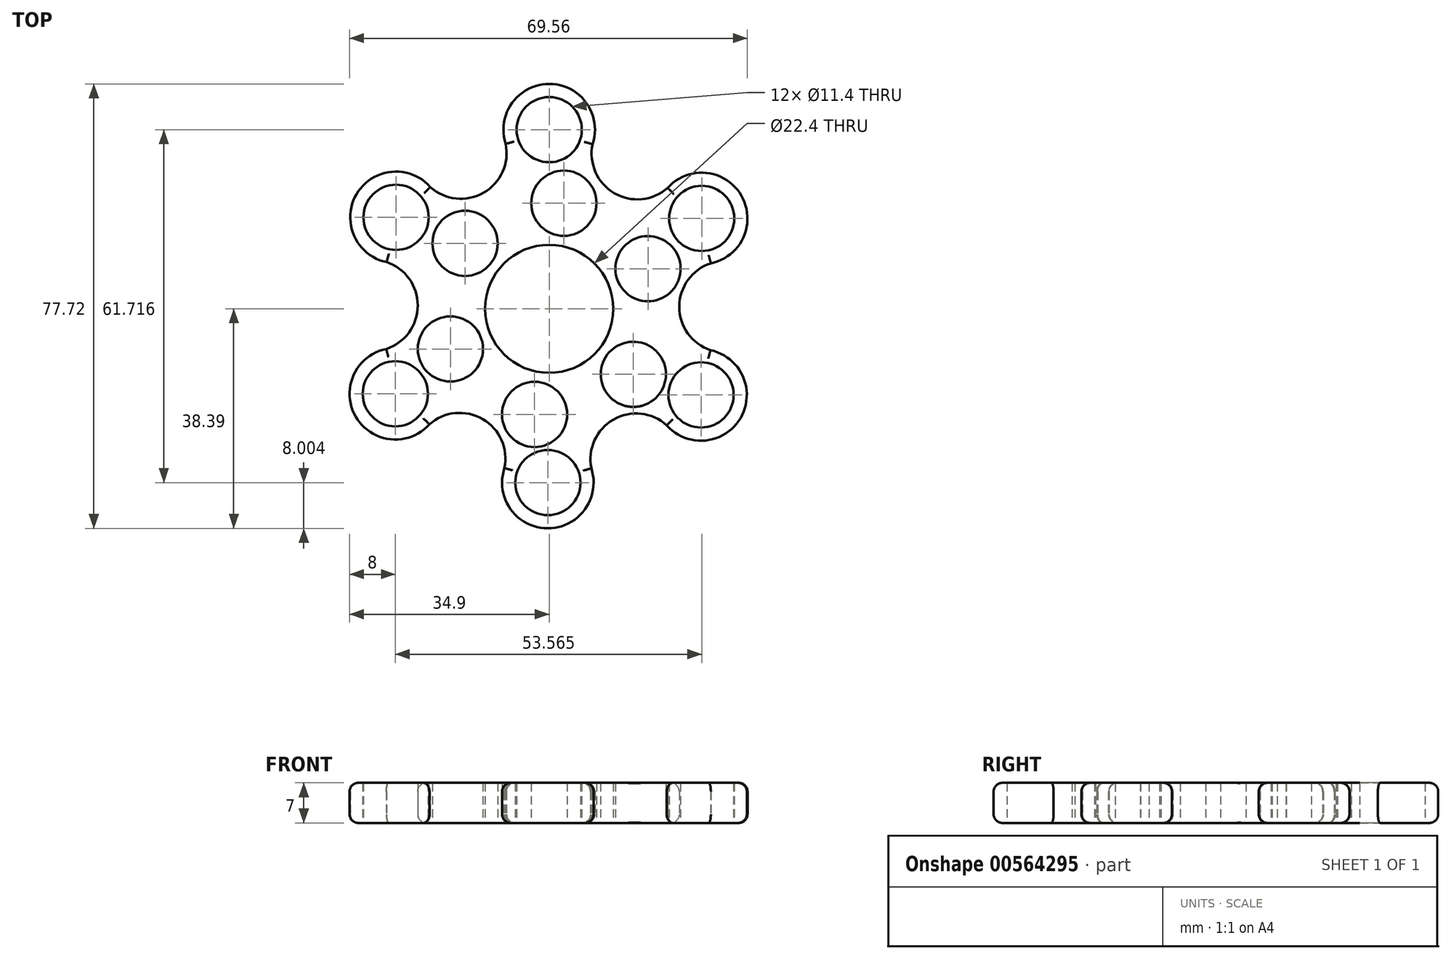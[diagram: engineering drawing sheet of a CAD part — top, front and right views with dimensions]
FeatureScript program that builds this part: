
annotation { "Feature Type Name" : "Feature", "Feature Type Description" : "" }
export const myFeature = defineFeature(function(context is Context, id is Id, definition is map)
    precondition{}
    {
        {
            var Q0;
            Q0=qCreatedBy(makeId("Top.planeOp"),FACE);
            var sketch = newSketch(context, id + "F0", { "sketchPlane" : qUnion([Q0])});
            skCircle(sketch, "E0", {"center": v(0, 0) * mm, "radius": 11.2 * mm});
            skArc(sketch, "E1", {"start": v(7.59, 28.79) * mm, "mid": v(0.03, 39.33) * mm, "end": v(-7.6, 28.85) * mm});
            skCircle(sketch, "E2", {"center": v(0, 31.33) * mm, "radius": 5.7 * mm});
            skArc(sketch, "E3.1.1", {"start": v(-20.79, 21.3) * mm, "mid": v(-11.47, 20.31) * mm, "end": v(-7.6, 28.85) * mm});
            skCircle(sketch, "E3.2.0", {"center": v(-26.78, 16) * mm, "radius": 5.7 * mm});
            skArc(sketch, "E3.2.1", {"start": v(-20.79, 21.3) * mm, "mid": v(-33.7, 20.03) * mm, "end": v(-28.43, 8.17) * mm});
            skArc(sketch, "E3.3.1", {"start": v(-28.5, -7.02) * mm, "mid": v(-22.98, 0.56) * mm, "end": v(-28.43, 8.17) * mm});
            skCircle(sketch, "E3.4.0", {"center": v(-26.9, -14.86) * mm, "radius": 5.7 * mm});
            skArc(sketch, "E3.4.1", {"start": v(-28.5, -7.02) * mm, "mid": v(-33.84, -18.83) * mm, "end": v(-20.95, -20.2) * mm});
            skArc(sketch, "E3.5.1", {"start": v(-7.82, -27.84) * mm, "mid": v(-11.62, -19.28) * mm, "end": v(-20.95, -20.2) * mm});
            skCircle(sketch, "E3.6.0", {"center": v(-0.24, -30.39) * mm, "radius": 5.7 * mm});
            skArc(sketch, "E3.6.1", {"start": v(-7.82, -27.84) * mm, "mid": v(-0.27, -38.39) * mm, "end": v(7.37, -27.9) * mm});
            skArc(sketch, "E3.7.1", {"start": v(20.55, -20.36) * mm, "mid": v(11.24, -19.37) * mm, "end": v(7.37, -27.9) * mm});
            skCircle(sketch, "E3.8.0", {"center": v(26.55, -15.06) * mm, "radius": 5.7 * mm});
            skArc(sketch, "E3.8.1", {"start": v(20.55, -20.36) * mm, "mid": v(33.46, -19.09) * mm, "end": v(28.2, -7.23) * mm});
            skArc(sketch, "E3.9.1", {"start": v(28.26, 7.96) * mm, "mid": v(22.74, 0.38) * mm, "end": v(28.2, -7.23) * mm});
            skCircle(sketch, "E3.10.0", {"center": v(26.66, 15.8) * mm, "radius": 5.7 * mm});
            skArc(sketch, "E3.10.1", {"start": v(28.26, 7.96) * mm, "mid": v(33.6, 19.77) * mm, "end": v(20.71, 21.14) * mm});
            skArc(sketch, "E3.11.1", {"start": v(7.59, 28.79) * mm, "mid": v(11.39, 20.22) * mm, "end": v(20.71, 21.14) * mm});
            skPoint(sketch, "E3.center", {"position": v(-0.12, 0.47) * mm});
            skCircle(sketch, "E4", {"center": v(2.56, 18.46) * mm, "radius": 5.7 * mm});
            skCircle(sketch, "E5.1.0", {"center": v(-14.71, 11.45) * mm, "radius": 5.7 * mm});
            skCircle(sketch, "E5.2.0", {"center": v(-17.27, -7.02) * mm, "radius": 5.7 * mm});
            skCircle(sketch, "E5.3.0", {"center": v(-2.56, -18.46) * mm, "radius": 5.7 * mm});
            skCircle(sketch, "E5.4.0", {"center": v(14.71, -11.45) * mm, "radius": 5.7 * mm});
            skCircle(sketch, "E5.5.0", {"center": v(17.27, 7.02) * mm, "radius": 5.7 * mm});
            skSolve(sketch);
        }
        {
            var Q0;
            Q0=makeQuery(id+"F0.imprint","IMPRINT",FACE,{"disambiguationData":[TD([[makeQuery(id+"F0.imprint","IMPRINT",EDGE,{"derivedFrom":sQuery(id+"F0.wireOp",EDGE,"E0")}),-1.0]])]});
            extrude(context, id + "F1", {"entities" : qUnion([Q0]), "depth" : 7 * mm, "offsetDistance" : 25 * mm});
        }
        {
            var Q0;
            Q0=makeQuery(id+"F1.opExtrude","CAP_EDGE",EDGE,{"disambiguationData":[OSD([sQuery(id+"F0.wireOp",EDGE,"E3.5.1")])],"isStart":false});
            var Q1;
            Q1=makeQuery(id+"F1.opExtrude","CAP_EDGE",EDGE,{"disambiguationData":[OSD([sQuery(id+"F0.wireOp",EDGE,"E3.4.1")])],"isStart":false});
            var Q2;
            Q2=makeQuery(id+"F1.opExtrude","CAP_EDGE",EDGE,{"disambiguationData":[OSD([sQuery(id+"F0.wireOp",EDGE,"E3.6.1")])],"isStart":false});
            var Q3;
            Q3=makeQuery(id+"F1.opExtrude","CAP_EDGE",EDGE,{"disambiguationData":[OSD([sQuery(id+"F0.wireOp",EDGE,"E3.7.1")])],"isStart":false});
            var Q4;
            Q4=makeQuery(id+"F1.opExtrude","CAP_EDGE",EDGE,{"disambiguationData":[OSD([sQuery(id+"F0.wireOp",EDGE,"E3.8.1")])],"isStart":false});
            var Q5;
            Q5=makeQuery(id+"F1.opExtrude","CAP_EDGE",EDGE,{"disambiguationData":[OSD([sQuery(id+"F0.wireOp",EDGE,"E3.9.1")])],"isStart":false});
            var Q6;
            Q6=makeQuery(id+"F1.opExtrude","CAP_EDGE",EDGE,{"disambiguationData":[OSD([sQuery(id+"F0.wireOp",EDGE,"E3.10.1")])],"isStart":false});
            var Q7;
            Q7=makeQuery(id+"F1.opExtrude","CAP_EDGE",EDGE,{"disambiguationData":[OSD([sQuery(id+"F0.wireOp",EDGE,"E3.11.1")])],"isStart":false});
            var Q8;
            Q8=makeQuery(id+"F1.opExtrude","CAP_EDGE",EDGE,{"disambiguationData":[OSD([sQuery(id+"F0.wireOp",EDGE,"E1")])],"isStart":false});
            var Q9;
            Q9=makeQuery(id+"F1.opExtrude","CAP_EDGE",EDGE,{"disambiguationData":[OSD([sQuery(id+"F0.wireOp",EDGE,"E3.1.1")])],"isStart":false});
            var Q10;
            Q10=makeQuery(id+"F1.opExtrude","CAP_EDGE",EDGE,{"disambiguationData":[OSD([sQuery(id+"F0.wireOp",EDGE,"E3.2.1")])],"isStart":false});
            var Q11;
            Q11=makeQuery(id+"F1.opExtrude","CAP_EDGE",EDGE,{"disambiguationData":[OSD([sQuery(id+"F0.wireOp",EDGE,"E3.3.1")])],"isStart":false});
            var Q12;
            Q12=makeQuery(id+"F1.opExtrude","CAP_EDGE",EDGE,{"disambiguationData":[OSD([sQuery(id+"F0.wireOp",EDGE,"E3.2.1")])],"isStart":true});
            var Q13;
            Q13=makeQuery(id+"F1.opExtrude","CAP_EDGE",EDGE,{"disambiguationData":[OSD([sQuery(id+"F0.wireOp",EDGE,"E3.3.1")])],"isStart":true});
            var Q14;
            Q14=makeQuery(id+"F1.opExtrude","CAP_EDGE",EDGE,{"disambiguationData":[OSD([sQuery(id+"F0.wireOp",EDGE,"E3.4.1")])],"isStart":true});
            var Q15;
            Q15=makeQuery(id+"F1.opExtrude","CAP_EDGE",EDGE,{"disambiguationData":[OSD([sQuery(id+"F0.wireOp",EDGE,"E3.5.1")])],"isStart":true});
            var Q16;
            Q16=makeQuery(id+"F1.opExtrude","CAP_EDGE",EDGE,{"disambiguationData":[OSD([sQuery(id+"F0.wireOp",EDGE,"E3.6.1")])],"isStart":true});
            var Q17;
            Q17=makeQuery(id+"F1.opExtrude","CAP_EDGE",EDGE,{"disambiguationData":[OSD([sQuery(id+"F0.wireOp",EDGE,"E3.7.1")])],"isStart":true});
            var Q18;
            Q18=makeQuery(id+"F1.opExtrude","CAP_EDGE",EDGE,{"disambiguationData":[OSD([sQuery(id+"F0.wireOp",EDGE,"E3.8.1")])],"isStart":true});
            var Q19;
            Q19=makeQuery(id+"F1.opExtrude","CAP_EDGE",EDGE,{"disambiguationData":[OSD([sQuery(id+"F0.wireOp",EDGE,"E3.9.1")])],"isStart":true});
            var Q20;
            Q20=makeQuery(id+"F1.opExtrude","CAP_EDGE",EDGE,{"disambiguationData":[OSD([sQuery(id+"F0.wireOp",EDGE,"E3.10.1")])],"isStart":true});
            var Q21;
            Q21=makeQuery(id+"F1.opExtrude","CAP_EDGE",EDGE,{"disambiguationData":[OSD([sQuery(id+"F0.wireOp",EDGE,"E3.11.1")])],"isStart":true});
            var Q22;
            Q22=makeQuery(id+"F1.opExtrude","CAP_EDGE",EDGE,{"disambiguationData":[OSD([sQuery(id+"F0.wireOp",EDGE,"E1")])],"isStart":true});
            var Q23;
            Q23=makeQuery(id+"F1.opExtrude","CAP_EDGE",EDGE,{"disambiguationData":[OSD([sQuery(id+"F0.wireOp",EDGE,"E3.1.1")])],"isStart":true});
            fillet(context, id + "F2", {"entities" : qUnion([Q0, Q1, Q2, Q3, Q4, Q5, Q6, Q7, Q8, Q9, Q10, Q11, Q12, Q13, Q14, Q15, Q16, Q17, Q18, Q19, Q20, Q21, Q22, Q23]), "radius" : 1.5 * mm, "tangentPropagation" : true, "allowEdgeOverflow" : false});
        }
    });
